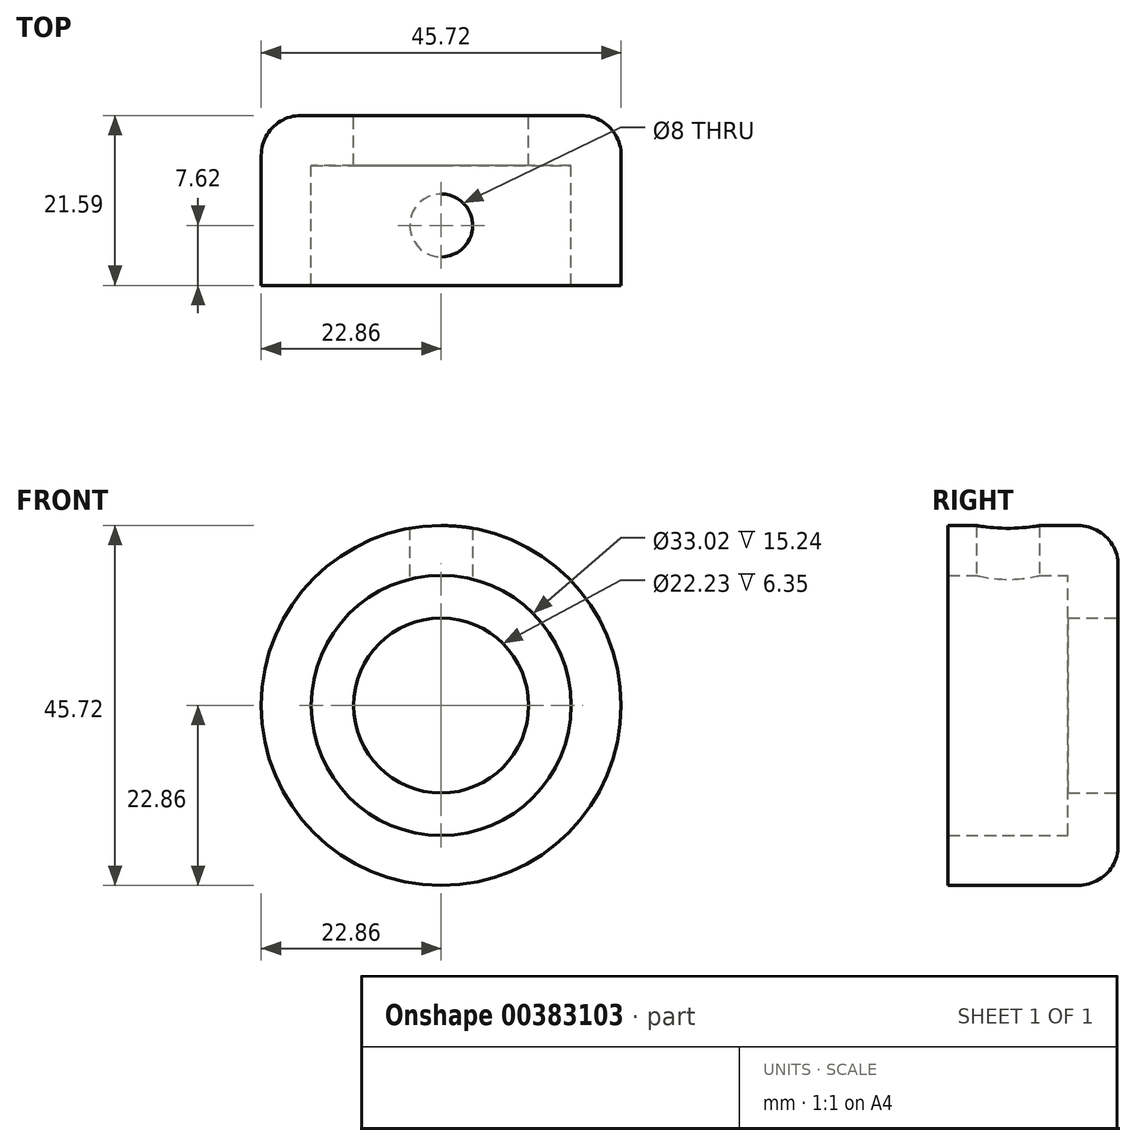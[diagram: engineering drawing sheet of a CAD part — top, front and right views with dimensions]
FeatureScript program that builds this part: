
annotation { "Feature Type Name" : "Feature", "Feature Type Description" : "" }
export const myFeature = defineFeature(function(context is Context, id is Id, definition is map)
    precondition{}
    {
        {
            var Q0;
            Q0=qCreatedBy(makeId("Front.planeOp"),FACE);
            var sketch = newSketch(context, id + "F0", { "sketchPlane" : qUnion([Q0])});
            skCircle(sketch, "E0", {"center": v(0, 0) * mm, "radius": 16.51 * mm});
            skCircle(sketch, "E1", {"center": v(0, 0) * mm, "radius": 22.86 * mm});
            skSolve(sketch);
        }
        {
            var Q0;
            Q0 = qSketchRegion(id + "F0", true);
            extrude(context, id + "F1", {"entities" : qUnion([Q0]), "endBound" : BoundingType.SYMMETRIC, "depth" : 15.24 * mm});
        }
        {
            var Q0;
            Q0=qCreatedBy(makeId("Top.planeOp"),FACE);
            var sketch = newSketch(context, id + "F2", { "sketchPlane" : qUnion([Q0])});
            skCircle(sketch, "E2", {"center": v(0, 0) * mm, "radius": 4 * mm});
            skSolve(sketch);
        }
        {
            var Q0;
            Q0 = qSketchRegion(id + "F2", true);
            extrude(context, id + "F3", {"entities" : qUnion([Q0]), "operationType" : NewBodyOperationType.REMOVE, "depth" : 77.22 * mm});
        }
        {
            var Q0;
            Q0=makeQuery(id+"F1.opExtrude","CAP_FACE",FACE,{"disambiguationData":[OSD([sQuery(id+"F0.wireOp",EDGE,"E0"),sQuery(id+"F0.wireOp",EDGE,"E1")])],"isStart":true});
            var sketch = newSketch(context, id + "F4", { "sketchPlane" : qUnion([Q0])});
            skCircle(sketch, "E3.0", {"center": v(0, 0) * mm, "radius": 22.86 * mm});
            skSolve(sketch);
        }
        {
            var Q0;
            Q0 = qSketchRegion(id + "F4", true);
            extrude(context, id + "F5", {"entities" : qUnion([Q0]), "operationType" : NewBodyOperationType.ADD, "depth" : 6.35 * mm});
        }
        {
            var Q0;
            Q0=makeQuery(id+"F5.opExtrude","CAP_FACE",FACE,{"disambiguationData":[OSD([sQuery(id+"F4.wireOp",EDGE,"E3.0")])],"isStart":false});
            var sketch = newSketch(context, id + "F6", { "sketchPlane" : qUnion([Q0])});
            skCircle(sketch, "E4", {"center": v(0, 0) * mm, "radius": 11.11 * mm});
            skSolve(sketch);
        }
        {
            var Q0;
            Q0 = qSketchRegion(id + "F6", true);
            extrude(context, id + "F7", {"entities" : qUnion([Q0]), "operationType" : NewBodyOperationType.REMOVE, "oppositeDirection" : true, "depth" : 25.4 * mm});
        }
        {
            var Q0;
            Q0=makeQuery(id+"F5.opExtrude","CAP_EDGE",EDGE,{"disambiguationData":[OSD([sQuery(id+"F4.wireOp",EDGE,"E3.0")])],"isStart":false});
            fillet(context, id + "F8", {"entities" : qUnion([Q0]), "radius" : 5.08 * mm, "tangentPropagation" : true, "allowEdgeOverflow" : false});
        }
    });
